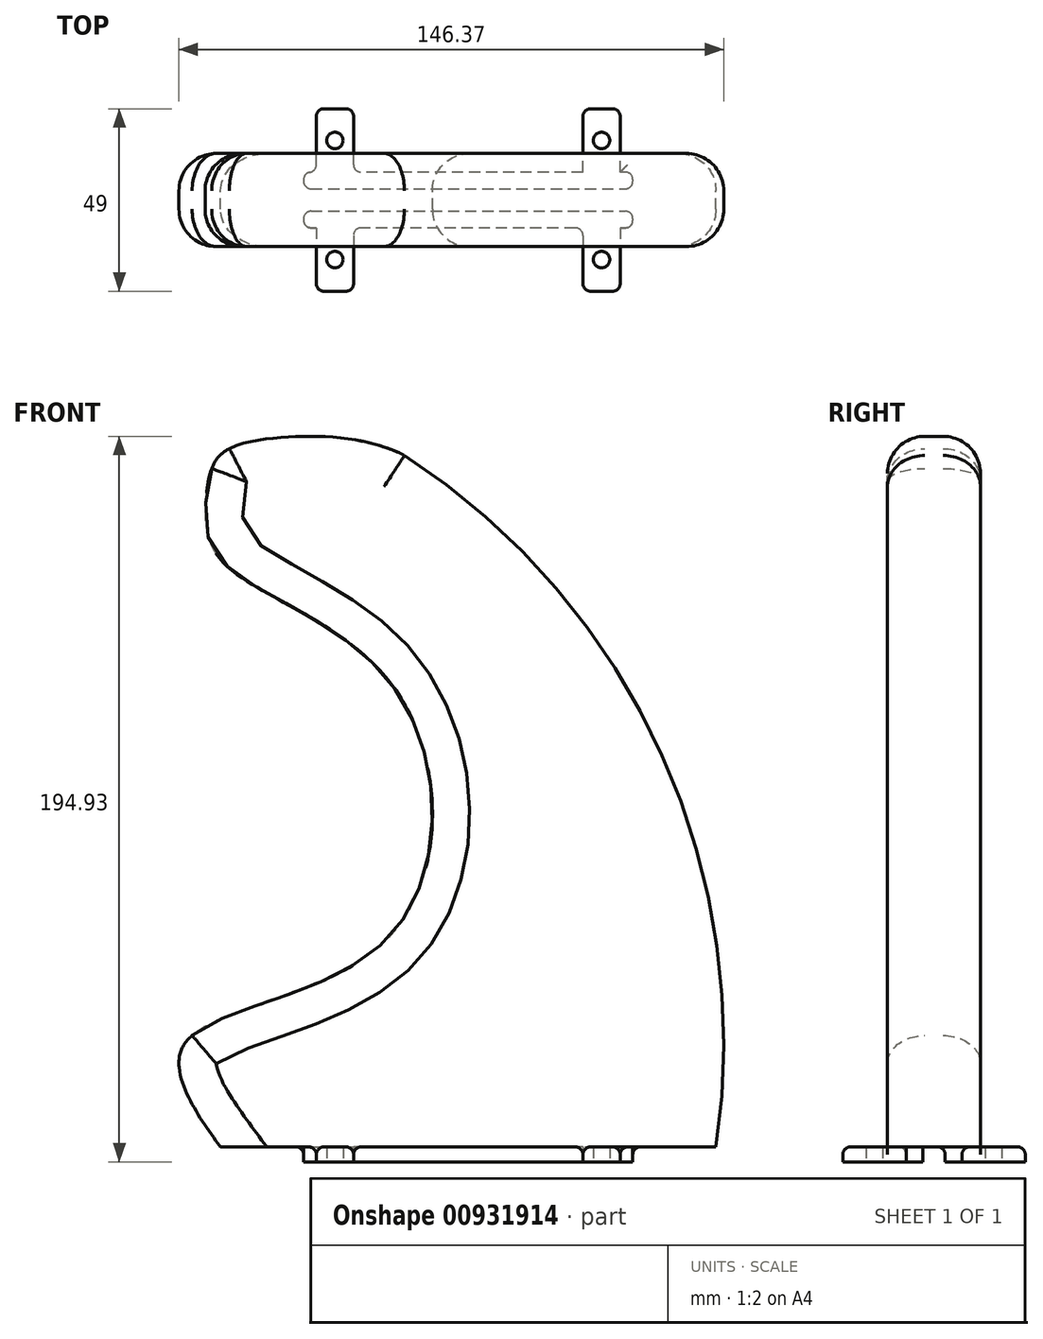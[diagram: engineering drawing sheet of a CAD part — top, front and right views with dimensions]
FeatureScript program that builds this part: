
annotation { "Feature Type Name" : "Feature", "Feature Type Description" : "" }
export const myFeature = defineFeature(function(context is Context, id is Id, definition is map)
    precondition{}
    {
        {
            var Q0;
            Q0=qCreatedBy(makeId("Front.planeOp"),FACE);
            var sketch = newSketch(context, id + "F0", { "sketchPlane" : qUnion([Q0])});
            skLineSegment(sketch, "E0.bottom", {"start": v(-76.45, 155.14) * mm, "end": v(73.55, 155.14) * mm});
            skLineSegment(sketch, "E0.top", {"start": v(-76.45, -54.86) * mm, "end": v(73.55, -54.86) * mm});
            skLineSegment(sketch, "E0.left", {"start": v(-76.45, 155.14) * mm, "end": v(-76.45, -54.86) * mm});
            skLineSegment(sketch, "E0.right", {"start": v(73.55, 155.14) * mm, "end": v(73.55, -54.86) * mm});
            skSolve(sketch);
        }
        {
            var Q0;
            Q0=qCreatedBy(makeId("Front.planeOp"),FACE);
            var sketch = newSketch(context, id + "F1", { "sketchPlane" : qUnion([Q0])});
            skLineSegment(sketch, "E1", {"start": v(-47, -36.88) * mm, "end": v(62.36, -36.88) * mm});
            skArc(sketch, "E2", {"start": v(62.36, -36.88) * mm, "mid": v(47.7, 68.69) * mm, "end": v(-22, 149.32) * mm});
            skLineSegment(sketch, "E3", {"start": v(11.54, -10.87) * mm, "end": v(-66.93, -10.87) * mm, "construction": true});
            skLineSegment(sketch, "E4", {"start": v(-17.6, 74.73) * mm, "end": v(-17.6, -3.44) * mm, "construction": true});
            skLineSegment(sketch, "E5", {"start": v(-47, -36.88) * mm, "end": v(-70.73, -36.88) * mm});
            skFitSpline(sketch, "E6", {"points": [v(-70.73, -36.88) * mm, v(-80.7, -9.65) * mm, v(-26.48, 18.52) * mm, v(-24.8, 87.45) * mm, v(-70.73, 120.95) * mm, v(-74.51, 138.6) * mm, v(-70.73, 149.12) * mm, v(-54.34, 153.74) * mm, v(-22, 149.32) * mm], "startDerivative": vector(-162.69, 221.36) * mm, "endDerivative": vector(260.78, -119.58) * mm});
            skSolve(sketch);
        }
        {
            var Q0;
            Q0 = qSketchRegion(id + "F1", true);
            extrude(context, id + "F2", {"entities" : qUnion([Q0]), "depth" : 25 * mm, "offsetDistance" : 25 * mm});
        }
        {
            var Q0;
            Q0=makeQuery(id+"F2.opExtrude","CAP_EDGE",EDGE,{"disambiguationData":[OSD([sQuery(id+"F1.wireOp",EDGE,"QmpCMBT4-KcOM-Yty2-izMm-gR6x4hVc0KeM")])],"isStart":true});
            var Q1;
            Q1=makeQuery(id+"F2.opExtrude","CAP_EDGE",EDGE,{"disambiguationData":[OSD([sQuery(id+"F1.wireOp",EDGE,"E2")])],"isStart":true});
            var Q2;
            Q2=makeQuery(id+"F2.opExtrude","CAP_EDGE",EDGE,{"disambiguationData":[OSD([sQuery(id+"F1.wireOp",EDGE,"QmpCMBT4-KcOM-Yty2-izMm-gR6x4hVc0KeM")])],"isStart":false});
            var Q3;
            Q3=makeQuery(id+"F2.opExtrude","CAP_EDGE",EDGE,{"disambiguationData":[OSD([sQuery(id+"F1.wireOp",EDGE,"8rwc7CL3-IXqj-vxCU-8WKL-maG0mN1euS7N")])],"isStart":true});
            var Q4;
            Q4=makeQuery(id+"F2.opExtrude","CAP_EDGE",EDGE,{"disambiguationData":[OSD([sQuery(id+"F1.wireOp",EDGE,"8rwc7CL3-IXqj-vxCU-8WKL-maG0mN1euS7N")])],"isStart":false});
            var Q5;
            Q5=makeQuery(id+"F2.opExtrude","CAP_EDGE",EDGE,{"disambiguationData":[OSD([sQuery(id+"F1.wireOp",EDGE,"E2")])],"isStart":false});
            fillet(context, id + "F3", {"entities" : qUnion([Q0, Q1, Q2, Q3, Q4, Q5]), "radius" : 10 * mm, "tangentPropagation" : true, "allowEdgeOverflow" : false});
        }
        {
            var Q0;
            Q0=makeQuery(id+"F3.opFillet","BLEND_EDGE",EDGE,{"blendedFrom":[makeQuery(id+"F2.opExtrude","CAP_EDGE",EDGE,{"disambiguationData":[OSD([sQuery(id+"F1.wireOp",EDGE,"E2")])],"isStart":true}),makeQuery(id+"F2.opExtrude","SWEPT_FACE",FACE,{"disambiguationData":[OSD([sQuery(id+"F1.wireOp",EDGE,"E6")])]})],"blendedInto":[makeQuery(id+"F2.opExtrude","SWEPT_FACE",FACE,{"disambiguationData":[OSD([sQuery(id+"F1.wireOp",EDGE,"E6")])]})]});
            fillet(context, id + "F4", {"entities" : qUnion([Q0]), "radius" : 10 * mm, "tangentPropagation" : true, "allowEdgeOverflow" : false});
        }
        {
            var Q0;
            Q0=makeQuery(id+"F2.opExtrude","SWEPT_FACE",FACE,{"disambiguationData":[OSD([sQuery(id+"F1.wireOp",EDGE,"E1"),sQuery(id+"F1.wireOp",EDGE,"E5")])]});
            cPlane(context, id + "F5", {"entities" : qUnion([Q0]), "cplaneType" : CPlaneType.OFFSET, "offset" : 0 * mm, "width" : 150 * mm, "height" : 150 * mm});
        }
        {
            var Q0;
            Q0=qCreatedBy(id+"F5.planeOp",FACE);
            var sketch = newSketch(context, id + "F6", { "sketchPlane" : qUnion([Q0])});
            skFitSpline(sketch, "E7.0", {"points": [v(-70.73, 10) * mm, v(-70.73, 9.26) * mm, v(-70.6, 8.35) * mm, v(-70.27, 7.3) * mm, v(-70, 6.6) * mm, v(-69.6, 5.78) * mm, v(-69, 4.86) * mm, v(-68.28, 4) * mm, v(-67.5, 3.24) * mm, v(-66.62, 2.55) * mm, v(-65.7, 1.94) * mm, v(-64.73, 1.42) * mm, v(-63.72, 0.98) * mm, v(-62.32, 0.5) * mm, v(-60.89, 0.19) * mm, v(-59.43, 0.03) * mm, v(-58.69, 0) * mm, v(-58.32, 0) * mm]});
            skLineSegment(sketch, "E7.1", {"start": v(-70.73, 15) * mm, "end": v(-70.73, 10) * mm});
            skFitSpline(sketch, "E7.2", {"points": [v(-58.32, 25) * mm, v(-59.06, 25) * mm, v(-60.52, 24.9) * mm, v(-62.3, 24.5) * mm, v(-63.71, 24.02) * mm, v(-64.72, 23.58) * mm, v(-65.69, 23.06) * mm, v(-66.6, 22.46) * mm, v(-67.48, 21.77) * mm, v(-68.27, 21) * mm, v(-68.98, 20.16) * mm, v(-69.6, 19.22) * mm, v(-70.08, 18.24) * mm, v(-70.39, 17.38) * mm, v(-70.56, 16.66) * mm, v(-70.7, 15.93) * mm, v(-70.73, 15.37) * mm, v(-70.73, 15) * mm]});
            skLineSegment(sketch, "E7.3", {"start": v(52.24, 25) * mm, "end": v(-58.32, 25) * mm});
            skFitSpline(sketch, "E7.4", {"points": [v(62.36, 15) * mm, v(62.36, 15.66) * mm, v(62.26, 16.64) * mm, v(61.93, 17.92) * mm, v(61.48, 19.17) * mm, v(60.85, 20.31) * mm, v(60.06, 21.38) * mm, v(59.38, 22.1) * mm, v(58.65, 22.76) * mm, v(57.85, 23.34) * mm, v(57, 23.84) * mm, v(56.1, 24.26) * mm, v(55.18, 24.59) * mm, v(54.2, 24.82) * mm, v(53.23, 24.97) * mm, v(52.57, 25) * mm, v(52.24, 25) * mm]});
            skLineSegment(sketch, "E7.5", {"start": v(62.36, 15) * mm, "end": v(62.36, 10) * mm});
            skFitSpline(sketch, "E7.6", {"points": [v(52.24, 0) * mm, v(52.57, 0) * mm, v(53.23, 0.03) * mm, v(54.2, 0.17) * mm, v(55.16, 0.4) * mm, v(56.1, 0.74) * mm, v(57, 1.15) * mm, v(57.84, 1.65) * mm, v(58.64, 2.23) * mm, v(59.38, 2.9) * mm, v(60.05, 3.62) * mm, v(60.64, 4.4) * mm, v(61.16, 5.25) * mm, v(61.59, 6.14) * mm, v(61.93, 7.06) * mm, v(62.17, 8.02) * mm, v(62.32, 9) * mm, v(62.36, 9.67) * mm, v(62.36, 10) * mm]});
            skLineSegment(sketch, "E7.7", {"start": v(-76.45, 0) * mm, "end": v(73.55, 0) * mm});
            skLineSegment(sketch, "E8", {"start": v(-70.73, 12.5) * mm, "end": v(62.36, 12.5) * mm});
            skLineSegment(sketch, "E9.bottom", {"start": v(-48.4, 9.5) * mm, "end": v(40.03, 9.5) * mm});
            skLineSegment(sketch, "E9.top", {"start": v(-48.4, 15.5) * mm, "end": v(40.03, 15.5) * mm});
            skLineSegment(sketch, "E9.left", {"start": v(-48.4, 9.5) * mm, "end": v(-48.4, 15.5) * mm});
            skLineSegment(sketch, "E9.right", {"start": v(40.03, 9.5) * mm, "end": v(40.03, 15.5) * mm});
            skPoint(sketch, "E9.middle", {"position": v(-4.19, 12.5) * mm});
            skLineSegment(sketch, "E10.bottom", {"start": v(40.03, 5) * mm, "end": v(-48.4, 5) * mm});
            skLineSegment(sketch, "E10.top", {"start": v(40.03, 20) * mm, "end": v(-48.4, 20) * mm});
            skLineSegment(sketch, "E10.left", {"start": v(40.03, 5) * mm, "end": v(40.03, 20) * mm});
            skLineSegment(sketch, "E10.right", {"start": v(-48.4, 5) * mm, "end": v(-48.4, 20) * mm});
            skSolve(sketch);
        }
        {
            var Q0;
            {var subQ0=sQuery(id+"F6.wireOp",EDGE,"E9.bottom");Q0=makeQuery(id+"F6.imprint","IMPRINT",FACE,{"disambiguationData":[TD([[makeQuery(id+"F6.imprint","IMPRINT",EDGE,{"derivedFrom":subQ0}),-1.0]])]});}
            var Q1;
            {var subQ0=sQuery(id+"F6.wireOp",EDGE,"E9.top");Q1=makeQuery(id+"F6.imprint","IMPRINT",FACE,{"disambiguationData":[TD([[makeQuery(id+"F6.imprint","IMPRINT",EDGE,{"derivedFrom":subQ0}),1.0]])]});}
            extrude(context, id + "F7", {"entities" : qUnion([Q0, Q1]), "operationType" : NewBodyOperationType.ADD, "depth" : 4 * mm, "offsetDistance" : 25 * mm});
        }
        {
            var Q0;
            Q0=makeQuery(id+"F7.opExtrude","CAP_FACE",FACE,{"disambiguationData":[OSD([sQuery(id+"F6.wireOp",EDGE,"E9.top"),sQuery(id+"F6.wireOp",EDGE,"E10.top"),sQuery(id+"F6.wireOp",EDGE,"E10.left"),sQuery(id+"F6.wireOp",EDGE,"E10.right")])],"isStart":false});
            cPlane(context, id + "F8", {"entities" : qUnion([Q0]), "cplaneType" : CPlaneType.OFFSET, "offset" : 0 * mm, "width" : 150 * mm, "height" : 150 * mm});
        }
        {
            var Q0;
            Q0=qCreatedBy(id+"F8.planeOp",FACE);
            var sketch = newSketch(context, id + "F9", { "sketchPlane" : qUnion([Q0])});
            skLineSegment(sketch, "E11.0.0", {"start": v(-48.4, 9.5) * mm, "end": v(-48.4, 5) * mm});
            skLineSegment(sketch, "E11.0.1", {"start": v(-48.4, 5) * mm, "end": v(40.03, 5) * mm});
            skLineSegment(sketch, "E11.0.2", {"start": v(40.03, 5) * mm, "end": v(40.03, 9.5) * mm});
            skLineSegment(sketch, "E11.0.3", {"start": v(40.03, 9.5) * mm, "end": v(-48.4, 9.5) * mm});
            skLineSegment(sketch, "E11.1.0", {"start": v(40.03, 15.5) * mm, "end": v(40.03, 20) * mm});
            skLineSegment(sketch, "E11.1.1", {"start": v(40.03, 20) * mm, "end": v(-48.4, 20) * mm});
            skLineSegment(sketch, "E11.1.2", {"start": v(-48.4, 20) * mm, "end": v(-48.4, 15.5) * mm});
            skLineSegment(sketch, "E11.1.3", {"start": v(-48.4, 15.5) * mm, "end": v(40.03, 15.5) * mm});
            skLineSegment(sketch, "E12.bottom", {"start": v(-45, 20) * mm, "end": v(-35, 20) * mm});
            skLineSegment(sketch, "E12.top", {"start": v(-45, 37) * mm, "end": v(-35, 37) * mm});
            skLineSegment(sketch, "E12.left", {"start": v(-45, 20) * mm, "end": v(-45, 37) * mm});
            skLineSegment(sketch, "E12.right", {"start": v(-35, 20) * mm, "end": v(-35, 37) * mm});
            skLineSegment(sketch, "E13", {"start": v(-45, 37) * mm, "end": v(-35, 20) * mm, "construction": true});
            skCircle(sketch, "E14", {"center": v(-40, 28.5) * mm, "radius": 2.2 * mm});
            skLineSegment(sketch, "E15", {"start": v(-4.19, 9.5) * mm, "end": v(-4.19, 15.5) * mm, "construction": true});
            skLineSegment(sketch, "E16", {"start": v(-4.19, 12.5) * mm, "end": v(36.8, 12.5) * mm, "construction": true});
            skLineSegment(sketch, "E17.MirrorCS", {"start": v(26.63, 20) * mm, "end": v(26.63, 37) * mm});
            skCircle(sketch, "E18.MirrorC", {"center": v(31.63, 28.5) * mm, "radius": 2.2 * mm});
            skLineSegment(sketch, "E19.MirrorCS", {"start": v(36.63, 20) * mm, "end": v(36.63, 37) * mm});
            skLineSegment(sketch, "E20.MirrorCS", {"start": v(36.63, 37) * mm, "end": v(26.63, 37) * mm});
            skLineSegment(sketch, "E21.MirrorCS", {"start": v(26.63, 5) * mm, "end": v(26.63, -12) * mm});
            skCircle(sketch, "E22.MirrorC", {"center": v(31.63, -3.5) * mm, "radius": 2.2 * mm});
            skLineSegment(sketch, "E23.MirrorCS", {"start": v(36.63, -12) * mm, "end": v(26.63, -12) * mm});
            skLineSegment(sketch, "E24.MirrorCS", {"start": v(36.63, 5) * mm, "end": v(36.63, -12) * mm});
            skLineSegment(sketch, "E25.MirrorCS", {"start": v(-35, 5) * mm, "end": v(-35, -12) * mm});
            skCircle(sketch, "E26.MirrorC", {"center": v(-40, -3.5) * mm, "radius": 2.2 * mm});
            skLineSegment(sketch, "E27.MirrorCS", {"start": v(-45, -12) * mm, "end": v(-35, -12) * mm});
            skLineSegment(sketch, "E28.MirrorCS", {"start": v(-45, 5) * mm, "end": v(-45, -12) * mm});
            skLineSegment(sketch, "E29", {"start": v(-45, 5) * mm, "end": v(-35, 5) * mm});
            skLineSegment(sketch, "E30", {"start": v(36.63, 20) * mm, "end": v(26.63, 20) * mm});
            skSolve(sketch);
        }
        {
            var Q0;
            {var subQ0=sQuery(id+"F9.wireOp",EDGE,"E25.MirrorCS");Q0=makeQuery(id+"F9.imprint","IMPRINT",FACE,{"disambiguationData":[TD([[makeQuery(id+"F9.imprint","IMPRINT",EDGE,{"derivedFrom":subQ0}),-1.0]])]});}
            var Q1;
            Q1=makeQuery(id+"F9.imprint","IMPRINT",FACE,{"disambiguationData":[TD([[makeQuery(id+"F9.imprint","IMPRINT",EDGE,{"derivedFrom":sQuery(id+"F9.wireOp",EDGE,"E12.top")}),-1.0]])]});
            var Q2;
            {var subQ1=sQuery(id+"F9.wireOp",EDGE,"E17.MirrorCS");Q2=makeQuery(id+"F9.imprint","IMPRINT",FACE,{"disambiguationData":[TD([[makeQuery(id+"F9.imprint","IMPRINT",EDGE,{"derivedFrom":subQ1}),-1.0]])]});}
            var Q3;
            {var subQ0=sQuery(id+"F9.wireOp",EDGE,"E21.MirrorCS");Q3=makeQuery(id+"F9.imprint","IMPRINT",FACE,{"disambiguationData":[TD([[makeQuery(id+"F9.imprint","IMPRINT",EDGE,{"derivedFrom":subQ0}),1.0]])]});}
            extrude(context, id + "F10", {"entities" : qUnion([Q0, Q1, Q2, Q3]), "operationType" : NewBodyOperationType.ADD, "oppositeDirection" : true, "depth" : 4 * mm, "offsetDistance" : 25 * mm});
        }
        {
            var Q0;
            {var subQ0=sQuery(id+"F9.wireOp",EDGE,"E19.MirrorCS");Q0=makeQuery(id+"F10.boolean.opBoolean","SPLIT",EDGE,{"disambiguationData":[topologyDisambiguationEdgeConnected([makeQuery(id+"F10.opExtrude","CAP_FACE",FACE,{"disambiguationData":[OSD([sQuery(id+"F9.wireOp",EDGE,"E11.1.1"),sQuery(id+"F9.wireOp",EDGE,"E17.MirrorCS"),sQuery(id+"F9.wireOp",EDGE,"E18.MirrorC"),subQ0,sQuery(id+"F9.wireOp",EDGE,"E20.MirrorCS")])],"isStart":false})])],"derivedFrom":makeQuery(id+"F10.opExtrude","CAP_EDGE",EDGE,{"disambiguationData":[OSD([subQ0])],"isStart":false})});}
            var Q1;
            {var subQ0=sQuery(id+"F9.wireOp",EDGE,"E24.MirrorCS");Q1=makeQuery(id+"F10.boolean.opBoolean","SPLIT",EDGE,{"disambiguationData":[topologyDisambiguationEdgeConnected([makeQuery(id+"F10.opExtrude","CAP_FACE",FACE,{"disambiguationData":[OSD([sQuery(id+"F9.wireOp",EDGE,"E11.0.1"),sQuery(id+"F9.wireOp",EDGE,"E21.MirrorCS"),sQuery(id+"F9.wireOp",EDGE,"E22.MirrorC"),sQuery(id+"F9.wireOp",EDGE,"E23.MirrorCS"),subQ0])],"isStart":false})])],"derivedFrom":makeQuery(id+"F10.opExtrude","CAP_EDGE",EDGE,{"disambiguationData":[OSD([subQ0])],"isStart":false})});}
            var Q2;
            {var subQ0=sQuery(id+"F9.wireOp",EDGE,"E12.right");Q2=makeQuery(id+"F10.boolean.opBoolean","SPLIT",EDGE,{"disambiguationData":[topologyDisambiguationEdgeConnected([makeQuery(id+"F10.opExtrude","CAP_FACE",FACE,{"disambiguationData":[OSD([sQuery(id+"F9.wireOp",EDGE,"E11.1.1"),sQuery(id+"F9.wireOp",EDGE,"E12.top"),sQuery(id+"F9.wireOp",EDGE,"E12.left"),subQ0,sQuery(id+"F9.wireOp",EDGE,"E14")])],"isStart":false})])],"derivedFrom":makeQuery(id+"F10.opExtrude","CAP_EDGE",EDGE,{"disambiguationData":[OSD([subQ0])],"isStart":false})});}
            var Q3;
            {var subQ0=sQuery(id+"F9.wireOp",EDGE,"E25.MirrorCS");Q3=makeQuery(id+"F10.boolean.opBoolean","SPLIT",EDGE,{"disambiguationData":[topologyDisambiguationEdgeConnected([makeQuery(id+"F10.opExtrude","CAP_FACE",FACE,{"disambiguationData":[OSD([sQuery(id+"F9.wireOp",EDGE,"E11.0.1"),subQ0,sQuery(id+"F9.wireOp",EDGE,"E26.MirrorC"),sQuery(id+"F9.wireOp",EDGE,"E27.MirrorCS"),sQuery(id+"F9.wireOp",EDGE,"E28.MirrorCS")])],"isStart":false})])],"derivedFrom":makeQuery(id+"F10.opExtrude","CAP_EDGE",EDGE,{"disambiguationData":[OSD([subQ0])],"isStart":false})});}
            var Q4;
            {var subQ0=sQuery(id+"F9.wireOp",EDGE,"E21.MirrorCS");Q4=makeQuery(id+"F10.boolean.opBoolean","SPLIT",EDGE,{"disambiguationData":[topologyDisambiguationEdgeConnected([makeQuery(id+"F10.opExtrude","CAP_FACE",FACE,{"disambiguationData":[OSD([sQuery(id+"F9.wireOp",EDGE,"E11.0.1"),subQ0,sQuery(id+"F9.wireOp",EDGE,"E22.MirrorC"),sQuery(id+"F9.wireOp",EDGE,"E23.MirrorCS"),sQuery(id+"F9.wireOp",EDGE,"E24.MirrorCS")])],"isStart":false})])],"derivedFrom":makeQuery(id+"F10.opExtrude","CAP_EDGE",EDGE,{"disambiguationData":[OSD([subQ0])],"isStart":false})});}
            var Q5;
            {var subQ0=sQuery(id+"F9.wireOp",EDGE,"E28.MirrorCS");Q5=makeQuery(id+"F10.boolean.opBoolean","SPLIT",EDGE,{"disambiguationData":[topologyDisambiguationEdgeConnected([makeQuery(id+"F10.opExtrude","CAP_FACE",FACE,{"disambiguationData":[OSD([sQuery(id+"F9.wireOp",EDGE,"E11.0.1"),sQuery(id+"F9.wireOp",EDGE,"E25.MirrorCS"),sQuery(id+"F9.wireOp",EDGE,"E26.MirrorC"),sQuery(id+"F9.wireOp",EDGE,"E27.MirrorCS"),subQ0])],"isStart":false})])],"derivedFrom":makeQuery(id+"F10.opExtrude","CAP_EDGE",EDGE,{"disambiguationData":[OSD([subQ0])],"isStart":false})});}
            var Q6;
            {var subQ0=sQuery(id+"F9.wireOp",EDGE,"E12.left");Q6=makeQuery(id+"F10.boolean.opBoolean","SPLIT",EDGE,{"disambiguationData":[topologyDisambiguationEdgeConnected([makeQuery(id+"F10.opExtrude","CAP_FACE",FACE,{"disambiguationData":[OSD([sQuery(id+"F9.wireOp",EDGE,"E11.1.1"),sQuery(id+"F9.wireOp",EDGE,"E12.top"),subQ0,sQuery(id+"F9.wireOp",EDGE,"E12.right"),sQuery(id+"F9.wireOp",EDGE,"E14")])],"isStart":false})])],"derivedFrom":makeQuery(id+"F10.opExtrude","CAP_EDGE",EDGE,{"disambiguationData":[OSD([subQ0])],"isStart":false})});}
            var Q7;
            {var subQ0=sQuery(id+"F9.wireOp",EDGE,"E17.MirrorCS");Q7=makeQuery(id+"F10.boolean.opBoolean","SPLIT",EDGE,{"disambiguationData":[topologyDisambiguationEdgeConnected([makeQuery(id+"F10.opExtrude","CAP_FACE",FACE,{"disambiguationData":[OSD([sQuery(id+"F9.wireOp",EDGE,"E11.1.1"),subQ0,sQuery(id+"F9.wireOp",EDGE,"E18.MirrorC"),sQuery(id+"F9.wireOp",EDGE,"E19.MirrorCS"),sQuery(id+"F9.wireOp",EDGE,"E20.MirrorCS")])],"isStart":false})])],"derivedFrom":makeQuery(id+"F10.opExtrude","CAP_EDGE",EDGE,{"disambiguationData":[OSD([subQ0])],"isStart":false})});}
            var Q8;
            Q8=makeQuery(id+"F10.opExtrude","CAP_EDGE",EDGE,{"disambiguationData":[OSD([sQuery(id+"F9.wireOp",EDGE,"E12.top")])],"isStart":false});
            var Q9;
            Q9=makeQuery(id+"F10.opExtrude","CAP_EDGE",EDGE,{"disambiguationData":[OSD([sQuery(id+"F9.wireOp",EDGE,"E20.MirrorCS")])],"isStart":false});
            var Q10;
            Q10=makeQuery(id+"F10.opExtrude","CAP_EDGE",EDGE,{"disambiguationData":[OSD([sQuery(id+"F9.wireOp",EDGE,"E27.MirrorCS")])],"isStart":false});
            var Q11;
            Q11=makeQuery(id+"F10.opExtrude","CAP_EDGE",EDGE,{"disambiguationData":[OSD([sQuery(id+"F9.wireOp",EDGE,"E23.MirrorCS")])],"isStart":false});
            var Q12;
            Q12=makeQuery(id+"F10.opExtrude","SWEPT_EDGE",EDGE,{"disambiguationData":[OSD([sQuery(id+"F9.wireOp",EDGE,"E25.MirrorCS"),sQuery(id+"F9.wireOp",EDGE,"E27.MirrorCS")])]});
            var Q13;
            Q13=makeQuery(id+"F10.opExtrude","SWEPT_EDGE",EDGE,{"disambiguationData":[OSD([sQuery(id+"F9.wireOp",EDGE,"E27.MirrorCS"),sQuery(id+"F9.wireOp",EDGE,"E28.MirrorCS")])]});
            var Q14;
            Q14=makeQuery(id+"F10.opExtrude","SWEPT_EDGE",EDGE,{"disambiguationData":[OSD([sQuery(id+"F9.wireOp",EDGE,"E23.MirrorCS"),sQuery(id+"F9.wireOp",EDGE,"E24.MirrorCS")])]});
            var Q15;
            Q15=makeQuery(id+"F10.opExtrude","SWEPT_EDGE",EDGE,{"disambiguationData":[OSD([sQuery(id+"F9.wireOp",EDGE,"E21.MirrorCS"),sQuery(id+"F9.wireOp",EDGE,"E23.MirrorCS")])]});
            var Q16;
            Q16=makeQuery(id+"F10.opExtrude","SWEPT_EDGE",EDGE,{"disambiguationData":[OSD([sQuery(id+"F9.wireOp",EDGE,"E19.MirrorCS"),sQuery(id+"F9.wireOp",EDGE,"E20.MirrorCS")])]});
            var Q17;
            Q17=makeQuery(id+"F10.opExtrude","SWEPT_EDGE",EDGE,{"disambiguationData":[OSD([sQuery(id+"F9.wireOp",EDGE,"E17.MirrorCS"),sQuery(id+"F9.wireOp",EDGE,"E20.MirrorCS")])]});
            var Q18;
            Q18=makeQuery(id+"F10.opExtrude","SWEPT_EDGE",EDGE,{"disambiguationData":[OSD([sQuery(id+"F9.wireOp",EDGE,"E12.top"),sQuery(id+"F9.wireOp",EDGE,"E12.left")])]});
            var Q19;
            Q19=makeQuery(id+"F10.opExtrude","SWEPT_EDGE",EDGE,{"disambiguationData":[OSD([sQuery(id+"F9.wireOp",EDGE,"E12.top"),sQuery(id+"F9.wireOp",EDGE,"E12.right")])]});
            var Q20;
            Q20=makeQuery(id+"F7.opExtrude","SWEPT_EDGE",EDGE,{"disambiguationData":[OSD([sQuery(id+"F6.wireOp",EDGE,"E10.bottom"),sQuery(id+"F6.wireOp",EDGE,"E10.left")])]});
            var Q21;
            Q21=makeQuery(id+"F7.opExtrude","SWEPT_EDGE",EDGE,{"disambiguationData":[OSD([sQuery(id+"F6.wireOp",EDGE,"E9.top"),sQuery(id+"F6.wireOp",EDGE,"E9.right"),sQuery(id+"F6.wireOp",EDGE,"E10.left")])]});
            var Q22;
            Q22=makeQuery(id+"F7.opExtrude","SWEPT_EDGE",EDGE,{"disambiguationData":[OSD([sQuery(id+"F6.wireOp",EDGE,"E10.top"),sQuery(id+"F6.wireOp",EDGE,"E10.left")])]});
            var Q23;
            Q23=makeQuery(id+"F7.opExtrude","SWEPT_EDGE",EDGE,{"disambiguationData":[OSD([sQuery(id+"F6.wireOp",EDGE,"E9.bottom"),sQuery(id+"F6.wireOp",EDGE,"E9.right"),sQuery(id+"F6.wireOp",EDGE,"E10.left")])]});
            var Q24;
            Q24=makeQuery(id+"F7.opExtrude","SWEPT_EDGE",EDGE,{"disambiguationData":[OSD([sQuery(id+"F6.wireOp",EDGE,"E9.bottom"),sQuery(id+"F6.wireOp",EDGE,"E9.left"),sQuery(id+"F6.wireOp",EDGE,"E10.right")])]});
            var Q25;
            Q25=makeQuery(id+"F7.opExtrude","SWEPT_EDGE",EDGE,{"disambiguationData":[OSD([sQuery(id+"F6.wireOp",EDGE,"E10.top"),sQuery(id+"F6.wireOp",EDGE,"E10.right")])]});
            var Q26;
            Q26=makeQuery(id+"F7.opExtrude","SWEPT_EDGE",EDGE,{"disambiguationData":[OSD([sQuery(id+"F6.wireOp",EDGE,"E10.bottom"),sQuery(id+"F6.wireOp",EDGE,"E10.right")])]});
            var Q27;
            Q27=makeQuery(id+"F7.opExtrude","SWEPT_EDGE",EDGE,{"disambiguationData":[OSD([sQuery(id+"F6.wireOp",EDGE,"E9.top"),sQuery(id+"F6.wireOp",EDGE,"E9.left"),sQuery(id+"F6.wireOp",EDGE,"E10.right")])]});
            fillet(context, id + "F11", {"entities" : qUnion([Q0, Q1, Q2, Q3, Q4, Q5, Q6, Q7, Q8, Q9, Q10, Q11, Q12, Q13, Q14, Q15, Q16, Q17, Q18, Q19, Q20, Q21, Q22, Q23, Q24, Q25, Q26, Q27]), "radius" : 2 * mm, "tangentPropagation" : true, "allowEdgeOverflow" : false});
        }
        {
            var Q0;
            Q0=makeQuery(id+"F10.opExtrude","SWEPT_EDGE",EDGE,{"disambiguationData":[OSD([sQuery(id+"F9.wireOp",EDGE,"E11.0.1"),sQuery(id+"F9.wireOp",EDGE,"E28.MirrorCS")])]});
            var Q1;
            Q1=makeQuery(id+"F10.opExtrude","SWEPT_EDGE",EDGE,{"disambiguationData":[OSD([sQuery(id+"F9.wireOp",EDGE,"E11.1.1"),sQuery(id+"F9.wireOp",EDGE,"E12.right")])]});
            var Q2;
            Q2=makeQuery(id+"F10.opExtrude","SWEPT_EDGE",EDGE,{"disambiguationData":[OSD([sQuery(id+"F9.wireOp",EDGE,"E11.1.1"),sQuery(id+"F9.wireOp",EDGE,"E17.MirrorCS")])]});
            var Q3;
            Q3=makeQuery(id+"F10.opExtrude","SWEPT_EDGE",EDGE,{"disambiguationData":[OSD([sQuery(id+"F9.wireOp",EDGE,"E11.0.1"),sQuery(id+"F9.wireOp",EDGE,"E25.MirrorCS")])]});
            fillet(context, id + "F12", {"entities" : qUnion([Q0, Q1, Q2, Q3]), "radius" : 2 * mm, "tangentPropagation" : true, "allowEdgeOverflow" : false});
        }
        {
            var Q0;
            {var subQ0=sQuery(id+"F9.wireOp",EDGE,"E24.MirrorCS");Q0=makeQuery(id+"F10.boolean.opBoolean","SPLIT",EDGE,{"disambiguationData":[topologyDisambiguationEdgeConnected([makeQuery(id+"F2.opExtrude","SWEPT_FACE",FACE,{"disambiguationData":[OSD([sQuery(id+"F1.wireOp",EDGE,"E1"),sQuery(id+"F1.wireOp",EDGE,"E5")])]})])],"derivedFrom":makeQuery(id+"F10.opExtrude","CAP_EDGE",EDGE,{"disambiguationData":[OSD([subQ0])],"isStart":false})});}
            var Q1;
            {var subQ0=sQuery(id+"F9.wireOp",EDGE,"E19.MirrorCS");Q1=makeQuery(id+"F10.boolean.opBoolean","SPLIT",EDGE,{"disambiguationData":[topologyDisambiguationEdgeConnected([makeQuery(id+"F2.opExtrude","SWEPT_FACE",FACE,{"disambiguationData":[OSD([sQuery(id+"F1.wireOp",EDGE,"E1"),sQuery(id+"F1.wireOp",EDGE,"E5")])]})])],"derivedFrom":makeQuery(id+"F10.opExtrude","CAP_EDGE",EDGE,{"disambiguationData":[OSD([subQ0])],"isStart":false})});}
            var Q2;
            {var subQ0=sQuery(id+"F9.wireOp",EDGE,"E21.MirrorCS");Q2=makeQuery(id+"F10.boolean.opBoolean","SPLIT",EDGE,{"disambiguationData":[topologyDisambiguationEdgeConnected([makeQuery(id+"F2.opExtrude","SWEPT_FACE",FACE,{"disambiguationData":[OSD([sQuery(id+"F1.wireOp",EDGE,"E1"),sQuery(id+"F1.wireOp",EDGE,"E5")])]})])],"derivedFrom":makeQuery(id+"F10.opExtrude","CAP_EDGE",EDGE,{"disambiguationData":[OSD([subQ0])],"isStart":false})});}
            var Q3;
            {var subQ0=sQuery(id+"F9.wireOp",EDGE,"E17.MirrorCS");Q3=makeQuery(id+"F10.boolean.opBoolean","SPLIT",EDGE,{"disambiguationData":[topologyDisambiguationEdgeConnected([makeQuery(id+"F2.opExtrude","SWEPT_FACE",FACE,{"disambiguationData":[OSD([sQuery(id+"F1.wireOp",EDGE,"E1"),sQuery(id+"F1.wireOp",EDGE,"E5")])]})])],"derivedFrom":makeQuery(id+"F10.opExtrude","CAP_EDGE",EDGE,{"disambiguationData":[OSD([subQ0])],"isStart":false})});}
            var Q4;
            {var subQ0=sQuery(id+"F9.wireOp",EDGE,"E12.left");Q4=makeQuery(id+"F10.boolean.opBoolean","SPLIT",EDGE,{"disambiguationData":[topologyDisambiguationEdgeConnected([makeQuery(id+"F2.opExtrude","SWEPT_FACE",FACE,{"disambiguationData":[OSD([sQuery(id+"F1.wireOp",EDGE,"E1"),sQuery(id+"F1.wireOp",EDGE,"E5")])]})])],"derivedFrom":makeQuery(id+"F10.opExtrude","CAP_EDGE",EDGE,{"disambiguationData":[OSD([subQ0])],"isStart":false})});}
            var Q5;
            {var subQ0=sQuery(id+"F9.wireOp",EDGE,"E28.MirrorCS");Q5=makeQuery(id+"F10.boolean.opBoolean","SPLIT",EDGE,{"disambiguationData":[topologyDisambiguationEdgeConnected([makeQuery(id+"F2.opExtrude","SWEPT_FACE",FACE,{"disambiguationData":[OSD([sQuery(id+"F1.wireOp",EDGE,"E1"),sQuery(id+"F1.wireOp",EDGE,"E5")])]})])],"derivedFrom":makeQuery(id+"F10.opExtrude","CAP_EDGE",EDGE,{"disambiguationData":[OSD([subQ0])],"isStart":false})});}
            var Q6;
            {var subQ0=sQuery(id+"F9.wireOp",EDGE,"E25.MirrorCS");Q6=makeQuery(id+"F10.boolean.opBoolean","SPLIT",EDGE,{"disambiguationData":[topologyDisambiguationEdgeConnected([makeQuery(id+"F2.opExtrude","SWEPT_FACE",FACE,{"disambiguationData":[OSD([sQuery(id+"F1.wireOp",EDGE,"E1"),sQuery(id+"F1.wireOp",EDGE,"E5")])]})])],"derivedFrom":makeQuery(id+"F10.opExtrude","CAP_EDGE",EDGE,{"disambiguationData":[OSD([subQ0])],"isStart":false})});}
            fillet(context, id + "F13", {"entities" : qUnion([Q0, Q1, Q2, Q3, Q4, Q5, Q6]), "radius" : 2 * mm, "tangentPropagation" : true, "allowEdgeOverflow" : false});
        }
    });
